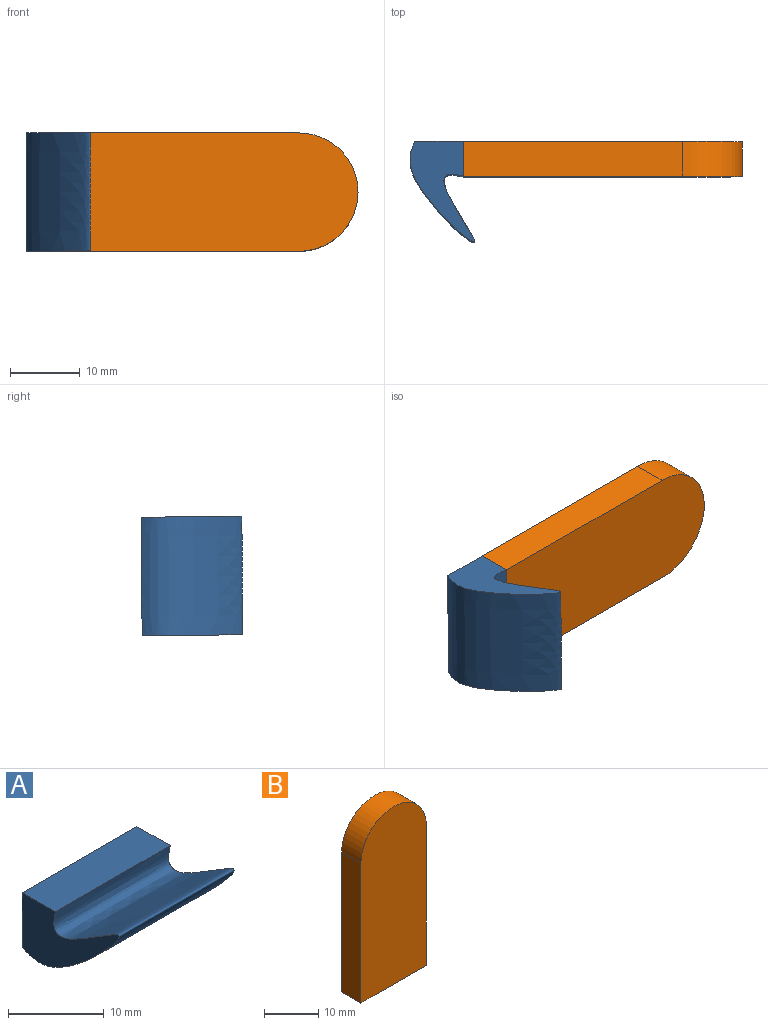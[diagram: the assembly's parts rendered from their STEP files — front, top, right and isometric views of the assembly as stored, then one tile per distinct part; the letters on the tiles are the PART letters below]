
ASSEMBLY  parts=2 mates=1
PART A: 5 faces, bbox 17x15.4x11.1 mm
  f0: extruded ~17x14.35mm, area 538.8mm2, adj f1,f2,f3,f4
  f1: plane 17x6.99mm, normal (0,1,0), area 118.8mm2, adj f0,f2,f3,f4
  f2: plane 17x4.94mm, normal (0,0.01,1), area 84mm2, adj f0,f1,f3,f4
  f3: plane 15.35x11.07mm, normal (1,0,0), area 62.1mm2, adj f0,f1,f2
  f4: plane 15.35x11.07mm, normal (-1,0,0), area 62.1mm2, adj f0,f1,f2
PART B: 6 faces, bbox 17x5x40 mm
  f0: plane 17x5mm, normal (0,0,-1), area 85mm2, adj f1,f3,f4,f5
  f1: plane 31.5x5mm, normal (1,0,0), area 157.5mm2, adj f0,f2,f4,f5
  f2: cylinder r=8.5mm len=17mm, axis (0,1,0), area 133.5mm2, adj f1,f3,f4,f5
  f3: plane 31.5x5mm, normal (-1,0,0), area 157.5mm2, adj f0,f2,f4,f5
  f4: plane 40x17mm, normal (0,-1,0), area 649mm2, adj f0,f1,f2,f3
  f5: plane 40x17mm, normal (0,1,0), area 649mm2, adj f0,f1,f2,f3
PLACE A rot(axis=(0,1,-0.01),90deg) t=(0.31,-0.04,-5.3)mm
PLACE B rot(axis=(0.71,0,0.71),179.7deg) t=(-15.33,-4.82,-5.38)mm
MATE fastened B.f0 <-> A.f2  axis (-1,0,0) through (-21.92,-2.32,-5.28)mm
